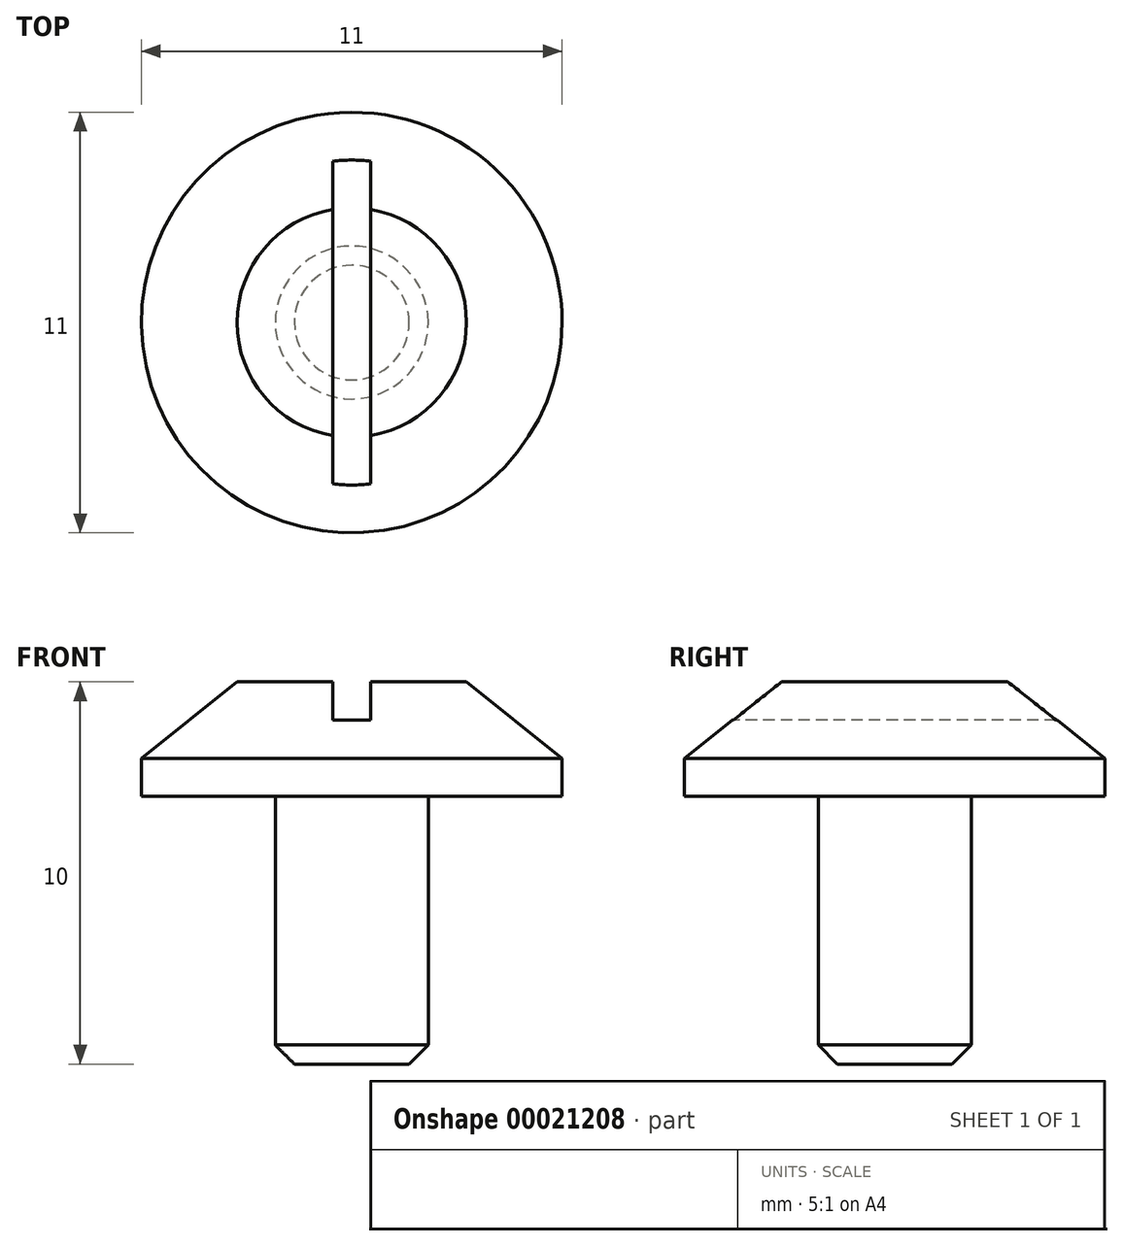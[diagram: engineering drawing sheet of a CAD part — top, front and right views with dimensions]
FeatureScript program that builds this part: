
annotation { "Feature Type Name" : "Feature", "Feature Type Description" : "" }
export const myFeature = defineFeature(function(context is Context, id is Id, definition is map)
    precondition{}
    {
        {
            var Q0;
            Q0=qCreatedBy(makeId("Top.planeOp"),FACE);
            var sketch = newSketch(context, id + "F0", { "sketchPlane" : qUnion([Q0])});
            skCircle(sketch, "E0", {"center": v(0, 0) * mm, "radius": 5.5 * mm});
            skSolve(sketch);
        }
        {
            var Q0;
            Q0=qSketchRegion(id+"F0",true);
            extrude(context, id + "F1", {"entities" : qUnion([Q0]), "depth" : 3 * mm});
        }
        {
            var Q0;
            Q0=makeQuery(id+"F1.opExtrude","CAP_EDGE",EDGE,{"disambiguationData":[OSD([sQuery(id+"F0.wireOp",EDGE,"E0")])],"isStart":false});
            chamfer(context, id + "F2", {"entities" : qUnion([Q0]), "chamferType" : ChamferType.TWO_OFFSETS, "width1" : 2.5 * mm, "oppositeDirection" : false, "width2" : 2 * mm, "tangentPropagation" : true});
        }
        {
            var Q0;
            Q0=qCreatedBy(makeId("Front.planeOp"),FACE);
            var sketch = newSketch(context, id + "F3", { "sketchPlane" : qUnion([Q0])});
            skLineSegment(sketch, "E1.0.0", {"start": v(-3, 3) * mm, "end": v(3, 3) * mm, "construction": true});
            skLineSegment(sketch, "E2.rect.bottom", {"start": v(0.5, 2) * mm, "end": v(-0.5, 2) * mm});
            skLineSegment(sketch, "E2.rect.top", {"start": v(0.5, 4) * mm, "end": v(-0.5, 4) * mm});
            skLineSegment(sketch, "E2.rect.left", {"start": v(0.5, 2) * mm, "end": v(0.5, 4) * mm});
            skLineSegment(sketch, "E2.rect.right", {"start": v(-0.5, 2) * mm, "end": v(-0.5, 4) * mm});
            skPoint(sketch, "E2.rect.middle", {"position": v(0, 3) * mm});
            skSolve(sketch);
        }
        {
            var Q0;
            Q0=qSketchRegion(id+"F3",true);
            extrude(context, id + "F4", {"entities" : qUnion([Q0]), "operationType" : NewBodyOperationType.REMOVE, "endBound" : BoundingType.THROUGH_ALL, "oppositeDirection" : true, "depth" : 25 * mm, "hasSecondDirection" : true, "secondDirectionBound" : SecondDirectionBoundingType.THROUGH_ALL, "secondDirectionOppositeDirection" : false, "secondDirectionDepth" : 25 * mm});
        }
        {
            var Q0;
            Q0=makeQuery(id+"F1.opExtrude","CAP_FACE",FACE,{"disambiguationData":[OSD([sQuery(id+"F0.wireOp",EDGE,"E0")])],"isStart":true});
            var sketch = newSketch(context, id + "F5", { "sketchPlane" : qUnion([Q0])});
            skCircle(sketch, "E3", {"center": v(0, 0) * mm, "radius": 2 * mm});
            skSolve(sketch);
        }
        {
            var Q0;
            Q0=qSketchRegion(id+"F5",true);
            extrude(context, id + "F6", {"entities" : qUnion([Q0]), "operationType" : NewBodyOperationType.ADD, "depth" : 7 * mm});
        }
        {
            var Q0;
            Q0=makeQuery(id+"F6.opExtrude","CAP_EDGE",EDGE,{"disambiguationData":[OSD([sQuery(id+"F5.wireOp",EDGE,"E3")])],"isStart":false});
            chamfer(context, id + "F7", {"entities" : qUnion([Q0]), "width" : 0.5 * mm, "tangentPropagation" : true});
        }
    });
